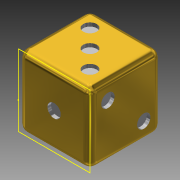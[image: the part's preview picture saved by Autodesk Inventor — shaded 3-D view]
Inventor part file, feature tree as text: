
AUTODESK INVENTOR PART (.ipt)
format: ipt  version: 2013 (Build 170138000, 138)  size: 249,856 bytes
history: native  units: in
note: dims shown in document units (in); Inventor stores cm internally (conversion verified against a paired STEP export)
features: sketch x8, extrude x7, fillet x2
ambient origin geometry x8: Origin, YZ Plane, XZ Plane, XY Plane, X Axis, Y Axis, Z Axis, Center Point
bodies: Solid1 (feature_tree)
feature tree (17):
  extrude  "Extrusion1"  Depth=1.0in
  sketch  "Sketch2"  dims[d2=1.0in d3=0.0in d4=0.187in]
  sketch  "Sketch3"  dims[d5=0.05in d6=0.0in d7=0.187in]
  extrude  "Extrusion2"  Depth=0.187in
  extrude  "Extrusion3"  Depth=0.187in
  extrude  "Extrusion4"  Depth=0.187in
  extrude  "Extrusion5"  Depth=0.187in
  extrude  "Extrusion6"  Depth=0.187in
  extrude  "Extrusion7"  Depth=0.05in TaperAngle=0.0deg
  fillet  "Fillet1"  Radius=0.187in
  fillet  "Fillet2"  Radius=0.187in
  sketch  "Sketch1"  dims[d0=1.0in d1=1.0in]
  sketch  "Sketch4"  dims[d8=0.187in d9=0.187in]
  sketch  "Sketch5"  dims[d10=0.05in d11=0.0in d12=0.187in]
  sketch  "Sketch6"  dims[d13=0.187in d14=0.187in]
  sketch  "Sketch7"  dims[d15=0.187in d16=0.05in d17=0.0in d18=0.187in d19=0.187in]
  sketch  "Sketch8"  dims[d20=0.187in d21=0.187in d22=0.187in d23=0.187in d24=0.05in d25=0.0in d26=0.25in d27=0.25in d28=0.25in d29=0.2498in d30=0.25in d31=0.2498in d32=0.25in d33=0.25in d34=0.5in d35=0.5in d36=0.187in d37=0.187in d38=0.187in d39=0.187in d40=0.187in d41=0.05in d42=0.0in d43=0.187in d44=0.187in d45=0.25in d46=0.25in d47=0.25in d48=0.25in d49=0.05in d50=0.0in d51=0.1in d52=0.1in]
